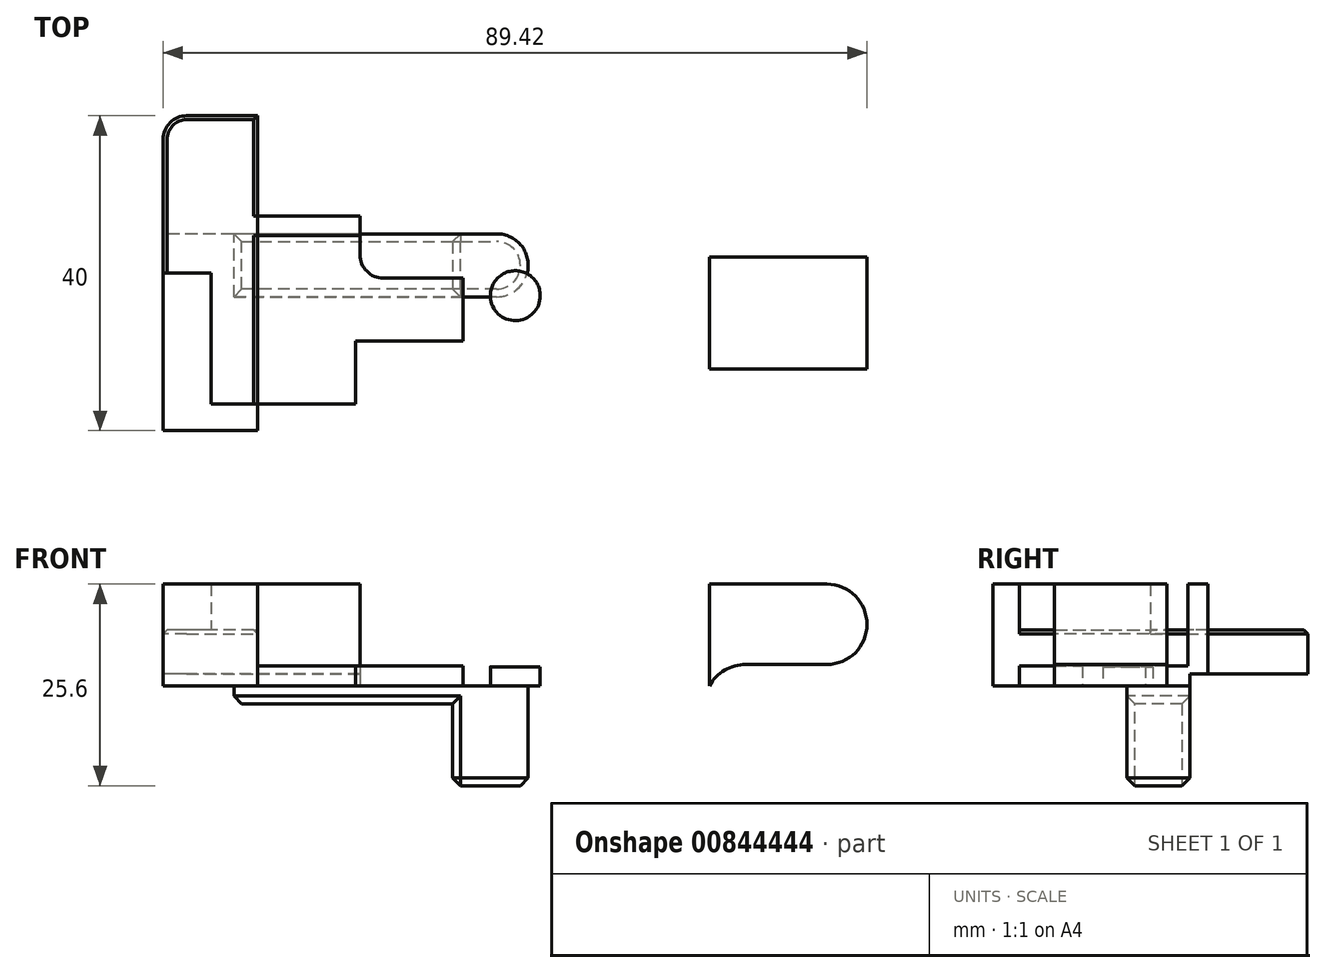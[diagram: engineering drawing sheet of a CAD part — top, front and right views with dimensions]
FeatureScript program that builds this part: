
annotation { "Feature Type Name" : "Feature", "Feature Type Description" : "" }
export const myFeature = defineFeature(function(context is Context, id is Id, definition is map)
    precondition{}
    {
        {
            var Q0;
            Q0=qCreatedBy(makeId("Top.planeOp"),FACE);
            var sketch = newSketch(context, id + "F0", { "sketchPlane" : qUnion([Q0])});
            skLineSegment(sketch, "E0.bottom", {"start": v(-26.12, 10.81) * mm, "end": v(31.27, 10.81) * mm});
            skLineSegment(sketch, "E0.top", {"start": v(-26.12, -16.45) * mm, "end": v(31.27, -16.45) * mm});
            skLineSegment(sketch, "E0.left", {"start": v(-26.12, 10.81) * mm, "end": v(-26.12, -16.45) * mm});
            skLineSegment(sketch, "E0.right", {"start": v(31.27, 10.81) * mm, "end": v(31.27, -16.45) * mm});
            skLineSegment(sketch, "E1.bottom", {"start": v(31.27, 5.63) * mm, "end": v(53.67, 5.63) * mm});
            skLineSegment(sketch, "E1.top", {"start": v(31.27, -8.62) * mm, "end": v(53.67, -8.62) * mm});
            skLineSegment(sketch, "E1.left", {"start": v(31.27, 5.63) * mm, "end": v(31.27, -8.62) * mm});
            skLineSegment(sketch, "E1.right", {"start": v(53.67, 5.63) * mm, "end": v(53.67, -8.62) * mm});
            skLineSegment(sketch, "E2.bottom", {"start": v(-26.12, -16.45) * mm, "end": v(-38.12, -16.45) * mm});
            skLineSegment(sketch, "E2.top", {"start": v(-26.12, 23.55) * mm, "end": v(-35.12, 23.55) * mm});
            skLineSegment(sketch, "E2.left", {"start": v(-26.12, -16.45) * mm, "end": v(-26.12, 23.55) * mm});
            skLineSegment(sketch, "E2.right", {"start": v(-38.12, -16.45) * mm, "end": v(-38.12, 20.55) * mm});
            skCircle(sketch, "E3", {"center": v(6.62, 0.7) * mm, "radius": 3.17 * mm});
            skCircle(sketch, "E4", {"center": v(18.45, -9.08) * mm, "radius": 4 * mm});
            skLineSegment(sketch, "E5.bottom", {"start": v(-26.12, 10.81) * mm, "end": v(-13.12, 10.81) * mm});
            skLineSegment(sketch, "E5.top", {"start": v(-26.12, -13.08) * mm, "end": v(-13.7, -13.08) * mm});
            skLineSegment(sketch, "E5.left", {"start": v(-26.12, 10.81) * mm, "end": v(-26.12, -13.08) * mm});
            skLineSegment(sketch, "E5.right", {"start": v(-13.12, 10.81) * mm, "end": v(-13.12, 5.92) * mm});
            skLineSegment(sketch, "E6.bottom", {"start": v(-10.12, 2.92) * mm, "end": v(0, 2.92) * mm});
            skLineSegment(sketch, "E6.top", {"start": v(-13.7, -5.08) * mm, "end": v(0, -5.08) * mm});
            skLineSegment(sketch, "E6.right", {"start": v(0, 2.92) * mm, "end": v(0, -5.08) * mm});
            skLineSegment(sketch, "E7", {"start": v(18.45, -5.08) * mm, "end": v(-13.7, -5.08) * mm});
            skLineSegment(sketch, "E8", {"start": v(18.45, -13.08) * mm, "end": v(-13.7, -13.08) * mm});
            skLineSegment(sketch, "E9", {"start": v(-13.7, -13.08) * mm, "end": v(-13.7, -5.08) * mm});
            skLineSegment(sketch, "E10", {"start": v(-26.12, -13.08) * mm, "end": v(-32.02, -13.08) * mm});
            skLineSegment(sketch, "E11", {"start": v(-32.02, -13.08) * mm, "end": v(-32.02, 3.55) * mm});
            skLineSegment(sketch, "E12", {"start": v(-32.02, 3.55) * mm, "end": v(-38.12, 3.55) * mm});
            skLineSegment(sketch, "E13", {"start": v(-13.12, 8.31) * mm, "end": v(-26.12, 8.31) * mm});
            skArc(sketch, "E14", {"start": v(-13.12, 5.92) * mm, "mid": v(-12.24, 3.8) * mm, "end": v(-10.12, 2.92) * mm});
            skLineSegment(sketch, "E15.trimOffspring", {"start": v(-13.7, -5.08) * mm, "end": v(-13.7, -13.08) * mm});
            skArc(sketch, "E16", {"start": v(-35.12, 23.55) * mm, "mid": v(-37.24, 22.68) * mm, "end": v(-38.12, 20.55) * mm});
            skSolve(sketch);
        }
        {
            var Q0;
            {var subQ10=sQuery(id+"F0.wireOp",EDGE,"E0.bottom");Q0=makeQuery(id+"F0.imprint","IMPRINT",FACE,{"disambiguationData":[TD([[makeQuery(id+"F0.imprint","IMPRINT",EDGE,{"derivedFrom":subQ10}),-1.0]])]});}
            var Q1;
            {var subQ2=sQuery(id+"F0.wireOp",EDGE,"E2.bottom");Q1=makeQuery(id+"F0.imprint","IMPRINT",FACE,{"disambiguationData":[TD([[makeQuery(id+"F0.imprint","IMPRINT",EDGE,{"derivedFrom":subQ2}),-1.0]])]});}
            var Q2;
            Q2=makeQuery(id+"F0.imprint","IMPRINT",FACE,{"disambiguationData":[TD([[makeQuery(id+"F0.imprint","IMPRINT",EDGE,{"derivedFrom":sQuery(id+"F0.wireOp",EDGE,"E1.bottom")}),-1.0]])]});
            extrude(context, id + "F1", {"entities" : qUnion([Q0, Q1, Q2]), "depth" : 12.9 * mm, "offsetDistance" : 25 * mm});
        }
        {
            var Q0;
            {var subQ1=sQuery(id+"F0.wireOp",EDGE,"E2.top");Q0=makeQuery(id+"F0.imprint","IMPRINT",FACE,{"disambiguationData":[TD([[makeQuery(id+"F0.imprint","IMPRINT",EDGE,{"derivedFrom":subQ1}),1.0]])]});}
            var Q1;
            {var subQ0=sQuery(id+"F0.wireOp",EDGE,"E5.bottom");Q1=makeQuery(id+"F0.imprint","IMPRINT",FACE,{"disambiguationData":[TD([[makeQuery(id+"F0.imprint","IMPRINT",EDGE,{"derivedFrom":subQ0}),-1.0]])]});}
            extrude(context, id + "F2", {"entities" : qUnion([Q0, Q1]), "operationType" : NewBodyOperationType.ADD, "depth" : 7.1 * mm, "offsetDistance" : 25 * mm});
        }
        {
            var Q0;
            {var subQ4=sQuery(id+"F0.wireOp",EDGE,"E5.top");Q0=makeQuery(id+"F0.imprint","IMPRINT",FACE,{"disambiguationData":[TD([[makeQuery(id+"F0.imprint","IMPRINT",EDGE,{"derivedFrom":subQ4}),1.0]])]});}
            var Q1;
            Q1=makeQuery(id+"F0.imprint","IMPRINT",FACE,{"disambiguationData":[TD([[makeQuery(id+"F0.imprint","IMPRINT",EDGE,{"derivedFrom":sQuery(id+"F0.wireOp",EDGE,"E6.bottom")}),-1.0]])]});
            extrude(context, id + "F3", {"entities" : qUnion([Q0, Q1]), "operationType" : NewBodyOperationType.ADD, "depth" : 2.5 * mm, "offsetDistance" : 25 * mm});
        }
        {
            var Q0;
            {var subQ0=sQuery(id+"F0.wireOp",EDGE,"E2.right");Q0=makeQuery(id+"F2.boolean.opBoolean","MERGE",FACE,{"derivedFrom":[makeQuery(id+"F1.opExtrude","SWEPT_FACE",FACE,{"disambiguationData":[OSD([subQ0])]}),makeQuery(id+"F2.opExtrude","SWEPT_FACE",FACE,{"disambiguationData":[OSD([subQ0])]})]});}
            var sketch = newSketch(context, id + "F4", { "sketchPlane" : qUnion([Q0])});
            skLineSegment(sketch, "E17", {"start": v(-8.56, 0) * mm, "end": v(-8.56, 1.5) * mm});
            skLineSegment(sketch, "E18", {"start": v(-8.56, 1.5) * mm, "end": v(-23.56, 1.5) * mm});
            skLineSegment(sketch, "E19", {"start": v(-23.56, 1.5) * mm, "end": v(-23.56, 0) * mm});
            skLineSegment(sketch, "E20", {"start": v(-23.56, 0) * mm, "end": v(-8.56, 0) * mm});
            skSolve(sketch);
        }
        {
            var Q0;
            {var subQ0=sQuery(id+"F4.wireOp",EDGE,"E17");Q0=makeQuery(id+"F4.imprint","IMPRINT",FACE,{"disambiguationData":[TD([[makeQuery(id+"F4.imprint","IMPRINT",EDGE,{"derivedFrom":subQ0}),1.0]])]});}
            var Q1;
            {var subQ0=sQuery(id+"F4.wireOp",EDGE,"E19");Q1=makeQuery(id+"F4.imprint","IMPRINT",FACE,{"disambiguationData":[TD([[makeQuery(id+"F4.imprint","IMPRINT",EDGE,{"derivedFrom":subQ0}),1.0]])]});}
            extrude(context, id + "F5", {"entities" : qUnion([Q0, Q1]), "operationType" : NewBodyOperationType.REMOVE, "oppositeDirection" : true, "depth" : 93.5 * mm, "offsetDistance" : 25 * mm});
        }
        {
            var Q0;
            {var subQ0=sQuery(id+"F0.wireOp",EDGE,"E14");var subQ1=sQuery(id+"F0.wireOp",EDGE,"E13");var subQ2=sQuery(id+"F0.wireOp",EDGE,"E7");var subQ3=sQuery(id+"F0.wireOp",EDGE,"E6.right");var subQ4=sQuery(id+"F0.wireOp",EDGE,"E6.bottom");var subQ5=sQuery(id+"F0.wireOp",EDGE,"E5.right");var subQ6=sQuery(id+"F0.wireOp",EDGE,"E5.left");var subQ7=sQuery(id+"F0.wireOp",EDGE,"E5.top");var subQ8=sQuery(id+"F0.wireOp",EDGE,"E12");var subQ9=sQuery(id+"F0.wireOp",EDGE,"E11");var subQ10=sQuery(id+"F0.wireOp",EDGE,"E10");var subQ11=sQuery(id+"F0.wireOp",EDGE,"E2.right");Q0=makeQuery(id+"F3.boolean.opBoolean","MERGE",FACE,{"derivedFrom":[makeQuery(id+"F2.boolean.opBoolean","MERGE",FACE,{"derivedFrom":[makeQuery(id+"F1.opExtrude","CAP_FACE",FACE,{"disambiguationData":[OSD([sQuery(id+"F0.wireOp",EDGE,"E0.bottom"),sQuery(id+"F0.wireOp",EDGE,"E0.top"),sQuery(id+"F0.wireOp",EDGE,"E0.right"),sQuery(id+"F0.wireOp",EDGE,"E1.bottom"),sQuery(id+"F0.wireOp",EDGE,"E1.top"),sQuery(id+"F0.wireOp",EDGE,"E1.right"),sQuery(id+"F0.wireOp",EDGE,"E2.bottom"),subQ11,sQuery(id+"F0.wireOp",EDGE,"E3"),sQuery(id+"F0.wireOp",EDGE,"E4"),subQ7,subQ5,subQ4,subQ3,subQ2,sQuery(id+"F0.wireOp",EDGE,"E8"),subQ10,subQ9,subQ8,subQ0])],"isStart":true}),makeQuery(id+"F2.opExtrude","CAP_FACE",FACE,{"disambiguationData":[OSD([sQuery(id+"F0.wireOp",EDGE,"E2.top"),sQuery(id+"F0.wireOp",EDGE,"E2.left"),subQ11,sQuery(id+"F0.wireOp",EDGE,"E5.bottom"),subQ6,subQ5,subQ10,subQ9,subQ8,subQ1,sQuery(id+"F0.wireOp",EDGE,"E16")])],"isStart":true})]}),makeQuery(id+"F3.opExtrude","CAP_FACE",FACE,{"disambiguationData":[OSD([subQ7,subQ6,subQ5,subQ4,subQ3,subQ2,subQ1,subQ0,sQuery(id+"F0.wireOp",EDGE,"E15.trimOffspring")])],"isStart":true})]});}
            var sketch = newSketch(context, id + "F6", { "sketchPlane" : qUnion([Q0])});
            skArc(sketch, "E21", {"start": v(4.26, -8.56) * mm, "mid": v(8.26, -4.56) * mm, "end": v(4.26, -0.56) * mm});
            skLineSegment(sketch, "E22", {"start": v(4.26, -0.56) * mm, "end": v(-29.12, -0.56) * mm});
            skLineSegment(sketch, "E23", {"start": v(-29.12, -0.56) * mm, "end": v(-29.12, -8.56) * mm});
            skLineSegment(sketch, "E24", {"start": v(-29.12, -8.56) * mm, "end": v(4.26, -8.56) * mm});
            skLineSegment(sketch, "E25", {"start": v(-1.34, -8.56) * mm, "end": v(-1.34, -0.56) * mm});
            skSolve(sketch);
        }
        {
            var Q0;
            {var subQ3=sQuery(id+"F6.wireOp",EDGE,"E25");Q0=makeQuery(id+"F6.imprint","IMPRINT",FACE,{"disambiguationData":[TD([[makeQuery(id+"F6.imprint","IMPRINT",EDGE,{"derivedFrom":subQ3}),-1.0]])]});}
            var Q1;
            {var subQ0=sQuery(id+"F6.wireOp",EDGE,"E22");var subQ1=sQuery(id+"F6.wireOp",EDGE,"E21");var subQ2=makeQuery(id+"F6.imprint","INTERSECT",VERTEX,{"derivedFrom":[subQ1,subQ0]});Q1=makeQuery(id+"F6.imprint","IMPRINT",FACE,{"disambiguationData":[TD([[makeQuery(id+"F6.imprint","IMPRINT",EDGE,{"disambiguationData":[TD([[subQ2,1.0]])],"derivedFrom":subQ1}),1.0]])]});}
            extrude(context, id + "F7", {"entities" : qUnion([Q0, Q1]), "operationType" : NewBodyOperationType.ADD, "depth" : 12.7 * mm, "offsetDistance" : 25 * mm});
        }
        {
            var Q0;
            {var subQ0=sQuery(id+"F6.wireOp",EDGE,"E23");Q0=makeQuery(id+"F6.imprint","IMPRINT",FACE,{"disambiguationData":[TD([[makeQuery(id+"F6.imprint","IMPRINT",EDGE,{"derivedFrom":subQ0}),1.0]])]});}
            extrude(context, id + "F8", {"entities" : qUnion([Q0]), "operationType" : NewBodyOperationType.ADD, "depth" : 2.3 * mm, "offsetDistance" : 25 * mm});
        }
        {
            var Q0;
            Q0=makeQuery(id+"F1.opExtrude","SWEPT_FACE",FACE,{"disambiguationData":[OSD([sQuery(id+"F0.wireOp",EDGE,"E1.top")])]});
            var sketch = newSketch(context, id + "F9", { "sketchPlane" : qUnion([Q0])});
            skLineSegment(sketch, "E26", {"start": v(53.67, 2.7) * mm, "end": v(35.91, 2.7) * mm});
            skArc(sketch, "E27", {"start": v(35.91, 2.7) * mm, "mid": v(33.23, 1.98) * mm, "end": v(31.27, 0) * mm});
            skCircle(sketch, "E28", {"center": v(46.2, 7.8) * mm, "radius": 5.1 * mm});
            skSolve(sketch);
        }
        {
            var Q0;
            {var subQ0=sQuery(id+"F9.wireOp",EDGE,"E26");Q0=makeQuery(id+"F9.imprint","IMPRINT",FACE,{"disambiguationData":[TD([[makeQuery(id+"F9.imprint","IMPRINT",EDGE,{"derivedFrom":subQ0}),1.0]])]});}
            var Q1;
            {var subQ0=sQuery(id+"F9.wireOp",EDGE,"E28");var subQ1=sQuery(id+"F0.wireOp",EDGE,"E1.top");var subQ2=makeQuery(id+"F1.opExtrude","CAP_EDGE",EDGE,{"disambiguationData":[OSD([subQ1])],"isStart":false});var subQ3=makeQuery(id+"F9.imprint","INTERSECT",VERTEX,{"derivedFrom":[subQ2,subQ0]});Q1=makeQuery(id+"F9.imprint","IMPRINT",FACE,{"disambiguationData":[TD([[makeQuery(id+"F9.imprint","IMPRINT",EDGE,{"disambiguationData":[TD([[subQ3,1.0]])],"derivedFrom":subQ0}),-1.0]])]});}
            var Q2;
            {var subQ0=sQuery(id+"F9.wireOp",EDGE,"E26");var subQ3=sQuery(id+"F9.wireOp",EDGE,"E28");var subQ4=makeQuery(id+"F9.imprint","INTERSECT",VERTEX,{"derivedFrom":[subQ0,subQ3]});Q2=makeQuery(id+"F9.imprint","IMPRINT",FACE,{"disambiguationData":[TD([[makeQuery(id+"F9.imprint","IMPRINT",EDGE,{"disambiguationData":[TD([[subQ4,1.0]])],"derivedFrom":subQ0}),-1.0]])]});}
            extrude(context, id + "F10", {"entities" : qUnion([Q0, Q1, Q2]), "operationType" : NewBodyOperationType.REMOVE, "oppositeDirection" : true, "depth" : 25 * mm, "offsetDistance" : 25 * mm});
        }
        {
            var Q0;
            Q0=makeQuery(id+"F0.imprint","IMPRINT",FACE,{"disambiguationData":[TD([[makeQuery(id+"F0.imprint","IMPRINT",EDGE,{"derivedFrom":sQuery(id+"F0.wireOp",EDGE,"E3")}),1.0]])]});
            extrude(context, id + "F11", {"entities" : qUnion([Q0]), "operationType" : NewBodyOperationType.ADD, "depth" : 2.4 * mm, "offsetDistance" : 25 * mm});
        }
        {
            var Q0;
            Q0=makeQuery(id+"F8.opExtrude","CAP_EDGE",EDGE,{"disambiguationData":[OSD([sQuery(id+"F6.wireOp",EDGE,"E22")])],"isStart":false});
            var Q1;
            Q1=makeQuery(id+"F8.opExtrude","CAP_EDGE",EDGE,{"disambiguationData":[OSD([sQuery(id+"F6.wireOp",EDGE,"E24")])],"isStart":false});
            var Q2;
            Q2=makeQuery(id+"F8.opExtrude","CAP_EDGE",EDGE,{"disambiguationData":[OSD([sQuery(id+"F6.wireOp",EDGE,"E23")])],"isStart":false});
            var Q3;
            Q3=makeQuery(id+"F7.opExtrude","CAP_EDGE",EDGE,{"disambiguationData":[OSD([sQuery(id+"F6.wireOp",EDGE,"E25")])],"isStart":false});
            var Q4;
            Q4=makeQuery(id+"F7.opExtrude","SWEPT_EDGE",EDGE,{"disambiguationData":[OSD([sQuery(id+"F6.wireOp",EDGE,"E22"),sQuery(id+"F6.wireOp",EDGE,"E25")])]});
            var Q5;
            Q5=makeQuery(id+"F7.opExtrude","SWEPT_EDGE",EDGE,{"disambiguationData":[OSD([sQuery(id+"F0.wireOp",EDGE,"E2.right"),sQuery(id+"F4.wireOp",EDGE,"E17"),sQuery(id+"F4.wireOp",EDGE,"E20"),sQuery(id+"F6.wireOp",EDGE,"E21"),sQuery(id+"F6.wireOp",EDGE,"E24")])]});
            var Q6;
            Q6=makeQuery(id+"F7.opExtrude","CAP_FACE",FACE,{"disambiguationData":[OSD([sQuery(id+"F6.wireOp",EDGE,"E21"),sQuery(id+"F6.wireOp",EDGE,"E22"),sQuery(id+"F6.wireOp",EDGE,"E24"),sQuery(id+"F6.wireOp",EDGE,"E25")])],"isStart":false});
            var Q7;
            Q7=makeQuery(id+"F7.opExtrude","SWEPT_EDGE",EDGE,{"disambiguationData":[OSD([sQuery(id+"F6.wireOp",EDGE,"E24"),sQuery(id+"F6.wireOp",EDGE,"E25")])]});
            var Q8;
            Q8=makeQuery(id+"F8.opExtrude","CAP_EDGE",EDGE,{"disambiguationData":[OSD([sQuery(id+"F6.wireOp",EDGE,"E25")])],"isStart":false});
            chamfer(context, id + "F12", {"entities" : qUnion([Q0, Q1, Q2, Q3, Q4, Q5, Q6, Q7, Q8]), "width" : 1 * mm, "tangentPropagation" : true});
        }
        {
            var Q0;
            Q0=makeQuery(id+"F2.opExtrude","CAP_EDGE",EDGE,{"disambiguationData":[OSD([sQuery(id+"F0.wireOp",EDGE,"E2.left")])],"isStart":false});
            var Q1;
            Q1=makeQuery(id+"F2.opExtrude","CAP_EDGE",EDGE,{"disambiguationData":[OSD([sQuery(id+"F0.wireOp",EDGE,"E5.left")])],"isStart":false});
            var Q2;
            Q2=makeQuery(id+"F2.opExtrude","CAP_EDGE",EDGE,{"disambiguationData":[OSD([sQuery(id+"F0.wireOp",EDGE,"E2.top")])],"isStart":false});
            chamfer(context, id + "F13", {"entities" : qUnion([Q0, Q1, Q2]), "width" : .5 * mm, "tangentPropagation" : true});
        }
    });
